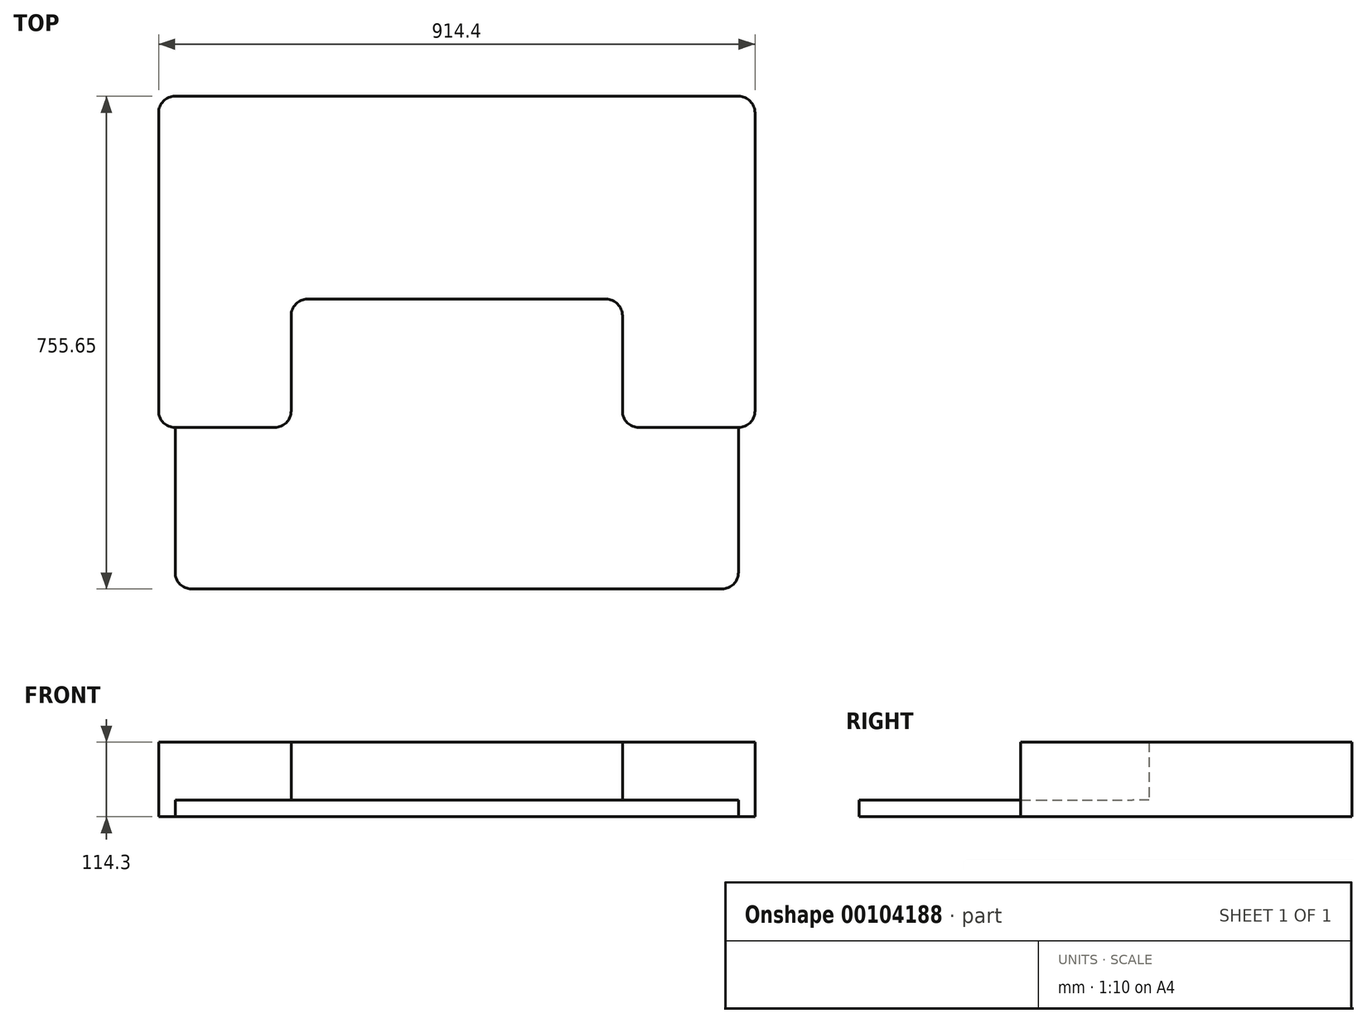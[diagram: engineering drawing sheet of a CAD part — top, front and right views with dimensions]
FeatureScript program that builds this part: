
annotation { "Feature Type Name" : "Feature", "Feature Type Description" : "" }
export const myFeature = defineFeature(function(context is Context, id is Id, definition is map)
    precondition{}
    {
        {
            var Q0;
            Q0=qCreatedBy(makeId("Top.planeOp"),FACE);
            var sketch = newSketch(context, id + "F0", { "sketchPlane" : qUnion([Q0])});
            skLineSegment(sketch, "E0", {"start": v(-457.2, 0) * mm, "end": v(457.2, 0) * mm});
            skLineSegment(sketch, "E1", {"start": v(-457.2, 0) * mm, "end": v(-457.2, -508) * mm});
            skLineSegment(sketch, "E2", {"start": v(-457.2, -508) * mm, "end": v(-254, -508) * mm});
            skLineSegment(sketch, "E3", {"start": v(-254, -508) * mm, "end": v(-254, -311.15) * mm});
            skLineSegment(sketch, "E4", {"start": v(-254, -311.15) * mm, "end": v(254, -311.15) * mm});
            skLineSegment(sketch, "E5", {"start": v(254, -311.15) * mm, "end": v(254, -508) * mm});
            skLineSegment(sketch, "E6", {"start": v(254, -508) * mm, "end": v(457.2, -508) * mm});
            skLineSegment(sketch, "E7", {"start": v(457.2, -508) * mm, "end": v(457.2, 0) * mm});
            skLineSegment(sketch, "E8", {"start": v(0, 0) * mm, "end": v(0, -311.15) * mm, "construction": true});
            skLineSegment(sketch, "E9", {"start": v(-431.8, -508) * mm, "end": v(-431.8, -755.65) * mm});
            skLineSegment(sketch, "E10", {"start": v(-431.8, -755.65) * mm, "end": v(431.8, -755.65) * mm});
            skLineSegment(sketch, "E11", {"start": v(431.8, -755.65) * mm, "end": v(431.8, -508) * mm});
            skPoint(sketch, "E12", {"position": v(0, -755.65) * mm});
            skSolve(sketch);
        }
        {
            var Q0;
            Q0=makeQuery(id+"F0.imprint","IMPRINT",FACE,{"disambiguationData":[TD([[makeQuery(id+"F0.imprint","IMPRINT",EDGE,{"derivedFrom":sQuery(id+"F0.wireOp",EDGE,"E0")}),-1.0]])]});
            extrude(context, id + "F1", {"entities" : qUnion([Q0]), "depth" : 114.3 * mm});
        }
        {
            var Q0;
            {var subQ5=sQuery(id+"F0.wireOp",EDGE,"E3");Q0=makeQuery(id+"F0.imprint","IMPRINT",FACE,{"disambiguationData":[TD([[makeQuery(id+"F0.imprint","IMPRINT",EDGE,{"derivedFrom":subQ5}),-1.0]])]});}
            extrude(context, id + "F2", {"entities" : qUnion([Q0]), "operationType" : NewBodyOperationType.ADD, "depth" : 25.4 * mm});
        }
        {
            var Q0;
            Q0=makeQuery(id+"F1.opExtrude","SWEPT_EDGE",EDGE,{"disambiguationData":[OSD([sQuery(id+"F0.wireOp",EDGE,"E1"),sQuery(id+"F0.wireOp",EDGE,"E2")])]});
            var Q1;
            Q1=makeQuery(id+"F2.opExtrude","SWEPT_EDGE",EDGE,{"disambiguationData":[OSD([sQuery(id+"F0.wireOp",EDGE,"E9"),sQuery(id+"F0.wireOp",EDGE,"E10")])]});
            var Q2;
            Q2=makeQuery(id+"F1.opExtrude","SWEPT_EDGE",EDGE,{"disambiguationData":[OSD([sQuery(id+"F0.wireOp",EDGE,"E2"),sQuery(id+"F0.wireOp",EDGE,"E3")])]});
            var Q3;
            Q3=makeQuery(id+"F1.opExtrude","SWEPT_EDGE",EDGE,{"disambiguationData":[OSD([sQuery(id+"F0.wireOp",EDGE,"E4"),sQuery(id+"F0.wireOp",EDGE,"E5")])]});
            var Q4;
            Q4=makeQuery(id+"F1.opExtrude","SWEPT_EDGE",EDGE,{"disambiguationData":[OSD([sQuery(id+"F0.wireOp",EDGE,"E5"),sQuery(id+"F0.wireOp",EDGE,"E6")])]});
            var Q5;
            Q5=makeQuery(id+"F1.opExtrude","SWEPT_EDGE",EDGE,{"disambiguationData":[OSD([sQuery(id+"F0.wireOp",EDGE,"E6"),sQuery(id+"F0.wireOp",EDGE,"E7")])]});
            var Q6;
            Q6=makeQuery(id+"F2.opExtrude","SWEPT_EDGE",EDGE,{"disambiguationData":[OSD([sQuery(id+"F0.wireOp",EDGE,"E10"),sQuery(id+"F0.wireOp",EDGE,"E11")])]});
            var Q7;
            Q7=makeQuery(id+"F1.opExtrude","SWEPT_EDGE",EDGE,{"disambiguationData":[OSD([sQuery(id+"F0.wireOp",EDGE,"E3"),sQuery(id+"F0.wireOp",EDGE,"E4")])]});
            var Q8;
            Q8=makeQuery(id+"F1.opExtrude","SWEPT_EDGE",EDGE,{"disambiguationData":[OSD([sQuery(id+"F0.wireOp",EDGE,"E0"),sQuery(id+"F0.wireOp",EDGE,"E7")])]});
            var Q9;
            Q9=makeQuery(id+"F1.opExtrude","SWEPT_EDGE",EDGE,{"disambiguationData":[OSD([sQuery(id+"F0.wireOp",EDGE,"E0"),sQuery(id+"F0.wireOp",EDGE,"E1")])]});
            fillet(context, id + "F3", {"entities" : qUnion([Q0, Q1, Q2, Q3, Q4, Q5, Q6, Q7, Q8, Q9]), "radius" : 25.4 * mm, "tangentPropagation" : true, "allowEdgeOverflow" : false});
        }
    });
